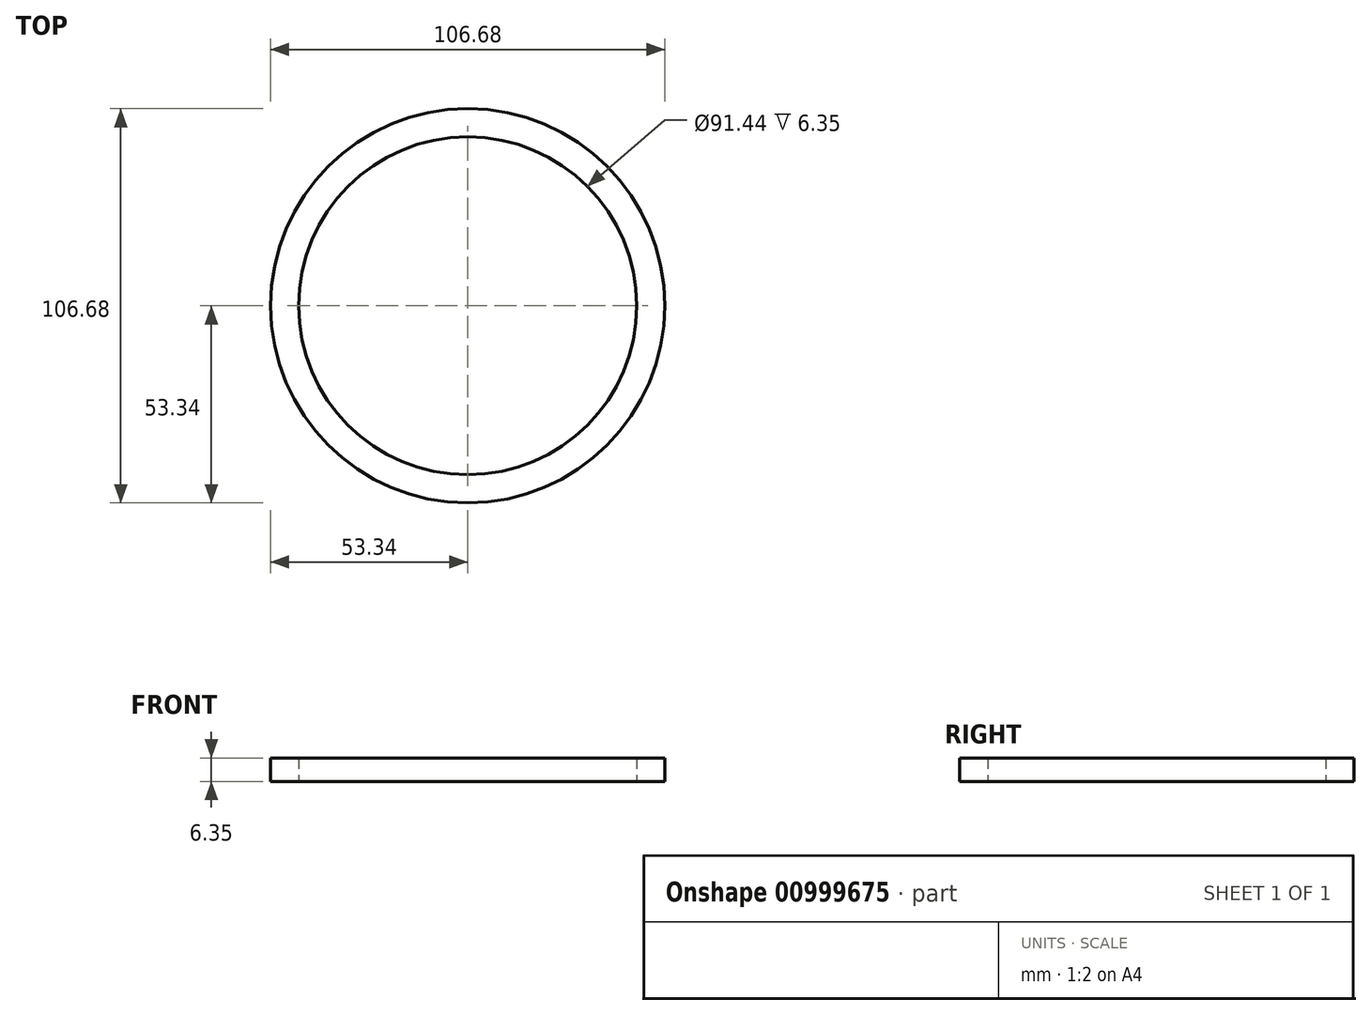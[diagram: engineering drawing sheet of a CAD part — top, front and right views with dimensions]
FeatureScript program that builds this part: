
annotation { "Feature Type Name" : "Feature", "Feature Type Description" : "" }
export const myFeature = defineFeature(function(context is Context, id is Id, definition is map)
    precondition{}
    {
        {
            var Q0;
            Q0=qCreatedBy(makeId("Top.planeOp"),FACE);
            var sketch = newSketch(context, id + "F0", { "sketchPlane" : qUnion([Q0])});
            skCircle(sketch, "E0", {"center": v(0, 0) * mm, "radius": 45.72 * mm});
            skCircle(sketch, "E1", {"center": v(0, 0) * mm, "radius": 53.34 * mm});
            skSolve(sketch);
        }
        {
            var Q0;
            Q0=makeQuery(id+"F0.imprint","IMPRINT",FACE,{"disambiguationData":[TD([[makeQuery(id+"F0.imprint","IMPRINT",EDGE,{"derivedFrom":sQuery(id+"F0.wireOp",EDGE,"E0")}),-1.0]])]});
            extrude(context, id + "F1", {"entities" : qUnion([Q0]), "depth" : 6.35 * mm, "offsetDistance" : 25.4 * mm});
        }
    });
